# Revit family: Accessory-Wall_Holder-KALLISTA-P24040-1
name_source: partatom
category: Specialty Equipment
units: mm (PartAtom-declared; Revit-internal decimal feet)

## family parameters
Cut with Voids When Loaded = No
Host = Face
Maintain Annotation Orientation = No
OmniClass Number = 23.31.25.00
Part Type = Normal
Room Calculation Point = No
Round Connector Dimension = Use Diameter
Shared = No

## types (4) — shared parameters
ADA Compliant = No
Assembly Code = C1030200
Date Modified = 06/28/2025
Default Elevation = 42"
Description = Fixed Wall Bracket
Height = 2 3/8"
Length = 2 7/16"
Manufacturer = Kallista Co.
Master Format 2014 = 10 28 00
Master Format 2014 Name = Toilet, Bath, and Laundry Accessories
Material = Premium Metal Construction
Product Name = Tuxedo
URL = https://www.kallista.com
WaterSense Certified = No
Width = 2 3/8"

## per-type parameters (varying)
| type | Finish | Model | Product Documentation Link | Product Page URL | Type |
| AD-Nickel Silver | Kallista-Metal-AD-Nickel_Silver | P24040-00-AD | https://techcomm.kohler.com | https://www.kallista.com | 1 |
| AG-Brushed Nickel | Kallista-Metal-AG-Brushed_Nickel | P24040-00-AG |  |  | 2 |
| CP-Chrome | Kallista-Metal-CP-Chrome | P24040-00-CP | https://techcomm.kohler.com | https://www.kallista.com | 3 |
| ULB-Unlaquered Brass | Kallista-Metal-ULB-Unlaquered_Brass | P24040-00-ULB | https://techcomm.kohler.com | https://www.kallista.com | 4 |

## geometry (parser evidence)
native form markers: Sweep x5
no freeform markers — native parametric forms only
